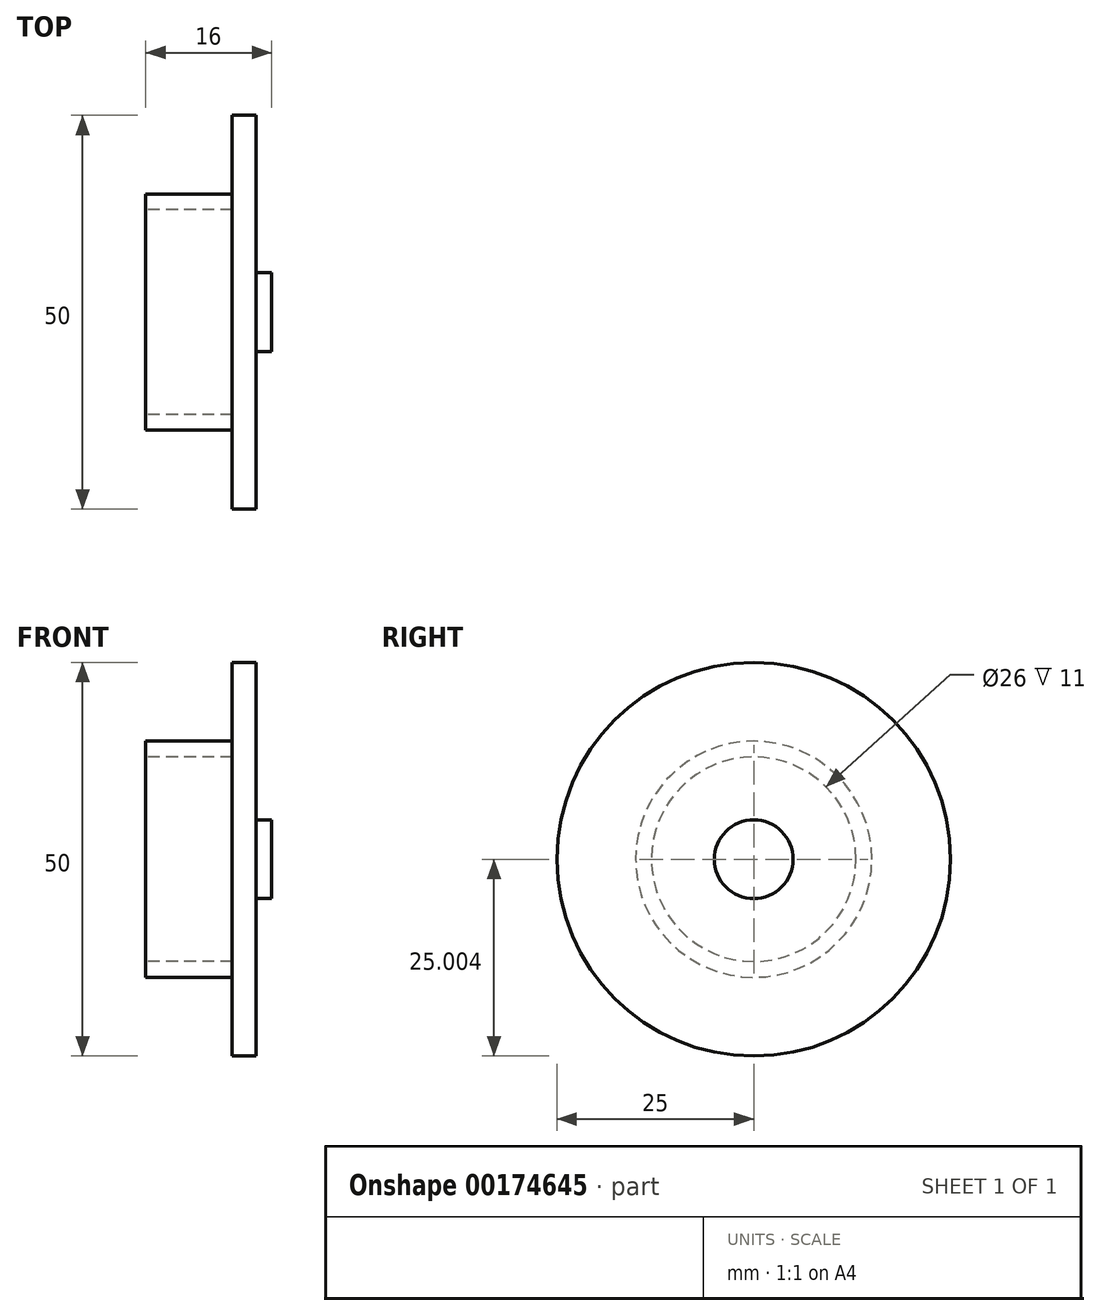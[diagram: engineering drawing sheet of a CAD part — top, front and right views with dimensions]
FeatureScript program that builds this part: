
annotation { "Feature Type Name" : "Feature", "Feature Type Description" : "" }
export const myFeature = defineFeature(function(context is Context, id is Id, definition is map)
    precondition{}
    {
        {
            var Q0;
            Q0=qCreatedBy(makeId("Front.planeOp"),FACE);
            var sketch = newSketch(context, id + "F0", { "sketchPlane" : qUnion([Q0])});
            skLineSegment(sketch, "E0.top", {"start": v(0, 31.24) * mm, "end": v(3, 31.24) * mm});
            skLineSegment(sketch, "E0.left", {"start": v(0, 6.24) * mm, "end": v(0, 31.24) * mm});
            skLineSegment(sketch, "E0.right", {"start": v(3, 6.24) * mm, "end": v(3, 31.24) * mm});
            skLineSegment(sketch, "E1", {"start": v(0, 6.24) * mm, "end": v(3, 6.24) * mm});
            skPoint(sketch, "E2.end.orphan", {"position": v(1.5, 6.24) * mm});
            skPoint(sketch, "E2.start.orphan", {"position": v(1.5, 0) * mm});
            skPoint(sketch, "E3.orphan", {"position": v(3, 0) * mm});
            skPoint(sketch, "E0.bottom.start.orphan", {"position": v(0, 0) * mm});
            skLineSegment(sketch, "E4.bottom", {"start": v(3, 6.24) * mm, "end": v(5, 6.24) * mm});
            skLineSegment(sketch, "E4.top", {"start": v(3, 11.24) * mm, "end": v(5, 11.24) * mm});
            skLineSegment(sketch, "E4.left", {"start": v(3, 6.24) * mm, "end": v(3, 11.24) * mm});
            skLineSegment(sketch, "E4.right", {"start": v(5, 6.24) * mm, "end": v(5, 11.24) * mm});
            skLineSegment(sketch, "E5.left", {"start": v(0, 31.24) * mm, "end": v(0, 22.42) * mm});
            skLineSegment(sketch, "E6.left", {"start": v(0, 22.42) * mm, "end": v(0, 20.39) * mm});
            skLineSegment(sketch, "E7.left", {"start": v(0, 31.24) * mm, "end": v(0, 29.6) * mm});
            skLineSegment(sketch, "E8.bottom", {"start": v(0, 29.6) * mm, "end": v(1.65, 29.6) * mm});
            skLineSegment(sketch, "E8.top", {"start": v(0, 22.9) * mm, "end": v(1.65, 22.9) * mm});
            skLineSegment(sketch, "E8.left", {"start": v(0, 29.6) * mm, "end": v(0, 22.9) * mm});
            skLineSegment(sketch, "E8.right", {"start": v(1.65, 29.6) * mm, "end": v(1.65, 22.9) * mm});
            skLineSegment(sketch, "E9.bottom", {"start": v(-10.97, 20.39) * mm, "end": v(-11, 20.39) * mm});
            skLineSegment(sketch, "E9.left", {"start": v(0, 20.39) * mm, "end": v(0, 18.35) * mm});
            skLineSegment(sketch, "E10.left", {"start": v(0, 20.39) * mm, "end": v(0, 18.39) * mm});
            skLineSegment(sketch, "E11.top", {"start": v(0, 21.24) * mm, "end": v(-0.77, 21.24) * mm});
            skLineSegment(sketch, "E11.left", {"start": v(0, 22.9) * mm, "end": v(0, 21.24) * mm});
            skLineSegment(sketch, "E12.bottom", {"start": v(0, 21.24) * mm, "end": v(-11, 21.24) * mm});
            skLineSegment(sketch, "E12.top", {"start": v(0, 19.24) * mm, "end": v(-11, 19.24) * mm});
            skLineSegment(sketch, "E12.left", {"start": v(0, 21.24) * mm, "end": v(0, 19.24) * mm});
            skLineSegment(sketch, "E12.right", {"start": v(-11, 21.24) * mm, "end": v(-11, 19.24) * mm});
            skLineSegment(sketch, "E13.left", {"start": v(1.65, 29.6) * mm, "end": v(1.65, 28.04) * mm});
            skLineSegment(sketch, "E14.left", {"start": v(1.65, 28.04) * mm, "end": v(1.65, 24.3) * mm});
            skSolve(sketch);
        }
        {
            var Q0;
            Q0 = qSketchRegion(id + "F0", true);
            var Q1;
            Q1=sQuery(id+"F0.wireOp",EDGE,"E4.bottom");
            revolve(context, id + "F1", {"entities" : qUnion([Q0]), "axis" : qUnion([Q1]), "revolveType" : RevolveType.FULL});
        }
    });
